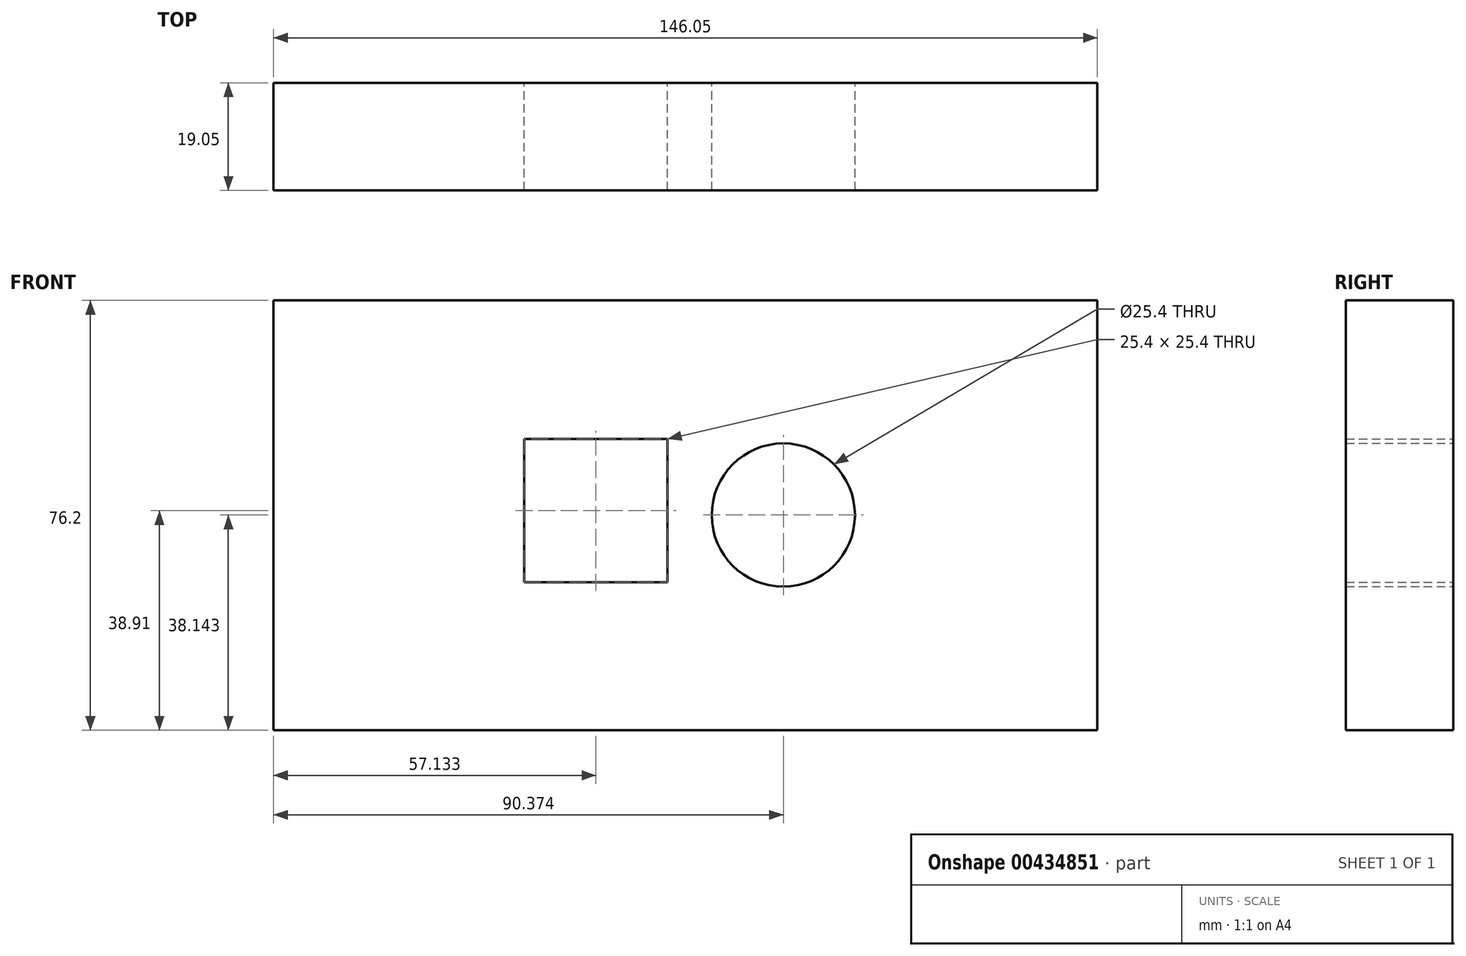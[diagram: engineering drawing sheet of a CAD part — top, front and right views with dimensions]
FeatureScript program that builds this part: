
annotation { "Feature Type Name" : "Feature", "Feature Type Description" : "" }
export const myFeature = defineFeature(function(context is Context, id is Id, definition is map)
    precondition{}
    {
        {
            var Q0;
            Q0=qCreatedBy(makeId("Front.planeOp"),FACE);
            var sketch = newSketch(context, id + "F0", { "sketchPlane" : qUnion([Q0])});
            skLineSegment(sketch, "E0", {"start": v(-76.68, 43.73) * mm, "end": v(69.37, 43.73) * mm});
            skLineSegment(sketch, "E1", {"start": v(-76.68, 43.73) * mm, "end": v(-76.68, -32.47) * mm});
            skLineSegment(sketch, "E2", {"start": v(-76.68, -32.47) * mm, "end": v(69.37, -32.47) * mm});
            skLineSegment(sketch, "E3", {"start": v(69.37, 43.73) * mm, "end": v(69.37, -32.47) * mm});
            skCircle(sketch, "E4", {"center": v(13.7, 5.67) * mm, "radius": 12.7 * mm});
            skLineSegment(sketch, "E5.bottom", {"start": v(-32.25, 19.14) * mm, "end": v(-6.85, 19.14) * mm});
            skLineSegment(sketch, "E5.top", {"start": v(-32.25, -6.26) * mm, "end": v(-6.85, -6.26) * mm});
            skLineSegment(sketch, "E5.left", {"start": v(-32.25, 19.14) * mm, "end": v(-32.25, -6.26) * mm});
            skLineSegment(sketch, "E5.right", {"start": v(-6.85, 19.14) * mm, "end": v(-6.85, -6.26) * mm});
            skSolve(sketch);
        }
        {
            var Q0;
            Q0 = qSketchRegion(id + "F0", true);
            extrude(context, id + "F1", {"entities" : qUnion([Q0]), "depth" : 19.05 * mm});
        }
    });
